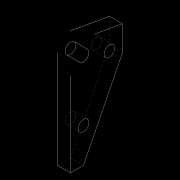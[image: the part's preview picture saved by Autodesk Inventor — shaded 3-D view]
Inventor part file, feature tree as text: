
AUTODESK INVENTOR PART (.ipt)
format: ipt  version: 2015 (Build 190159000, 159)  size: 112,640 bytes
history: native  units: mm
features: other x2, extrude x1, fillet x1, hole x1, imported_body x1
ambient origin geometry x8: Origin, YZ Plane, XZ Plane, XY Plane, X Axis, Y Axis, Z Axis, Center Point
bodies: Solid1 (feature_tree)
feature tree (6):
  other  "VibroKnuckle"
  extrude  "BaseFeature"  Depth=12.0mm
  fillet  "BaseFilletsFeature"  Radius=13.962634mm
  hole  "BaseHolesFeature"  [1 undecoded]
  imported_body  "Base"
  other  "BaseHoles"
note: 1 required parameter value undecoded (feature->parameter linkage not recoverable at this tier; creation-order binding heuristic only, values carry confidence <= 0.55)
